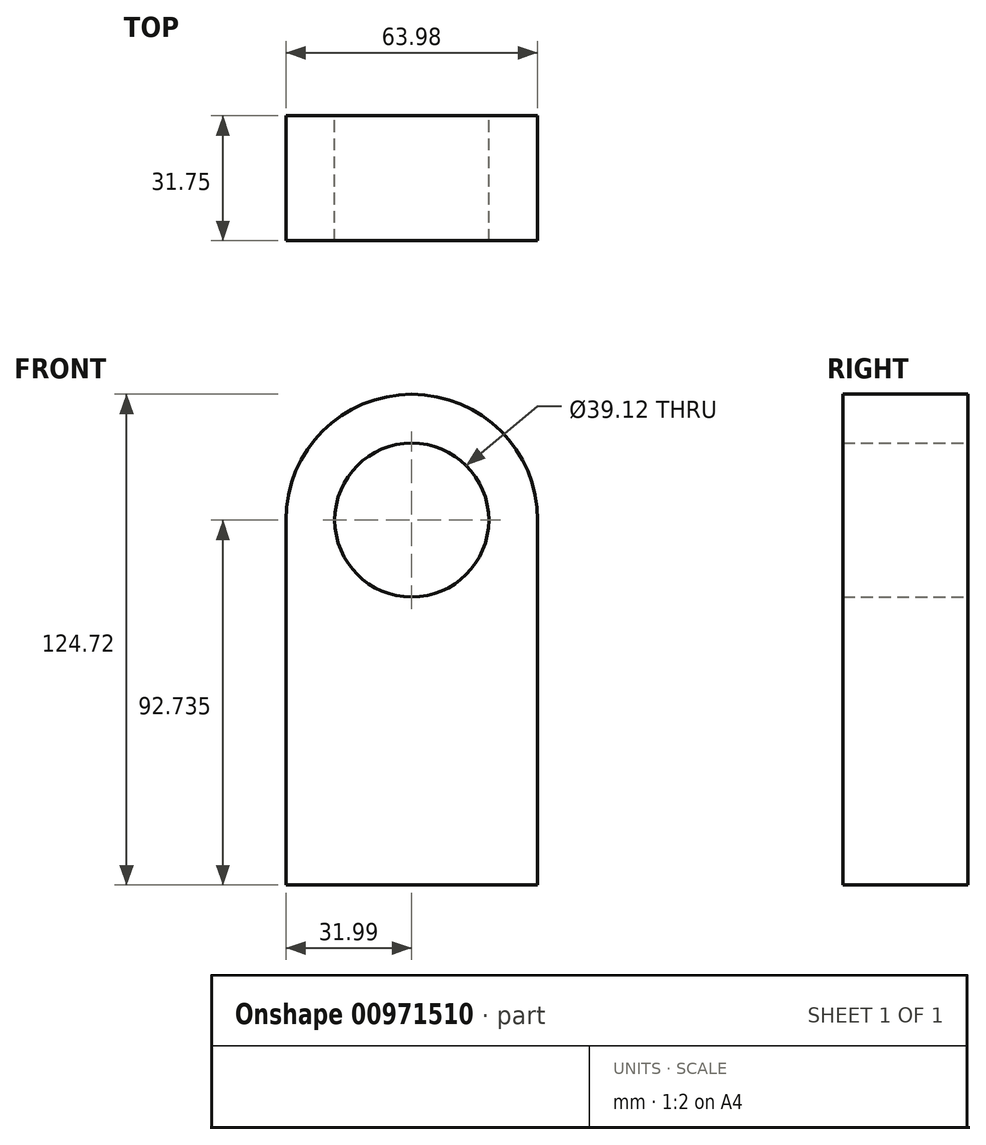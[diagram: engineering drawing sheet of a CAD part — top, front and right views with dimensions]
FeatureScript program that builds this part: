
annotation { "Feature Type Name" : "Feature", "Feature Type Description" : "" }
export const myFeature = defineFeature(function(context is Context, id is Id, definition is map)
    precondition{}
    {
        {
            var Q0;
            Q0=qCreatedBy(makeId("Front.planeOp"),FACE);
            var sketch = newSketch(context, id + "F0", { "sketchPlane" : qUnion([Q0])});
            skLineSegment(sketch, "E0.top", {"start": v(-31.99, -46.37) * mm, "end": v(31.99, -46.37) * mm});
            skLineSegment(sketch, "E0.left", {"start": v(-31.99, 46.37) * mm, "end": v(-31.99, -46.37) * mm});
            skLineSegment(sketch, "E0.right", {"start": v(31.99, 46.37) * mm, "end": v(31.99, -46.37) * mm});
            skPoint(sketch, "E0.middle", {"position": v(0, 0) * mm});
            skArc(sketch, "E1", {"start": v(31.99, 46.37) * mm, "mid": v(0, 78.35) * mm, "end": v(-31.99, 46.37) * mm});
            skCircle(sketch, "E2", {"center": v(0, 46.37) * mm, "radius": 19.56 * mm});
            skSolve(sketch);
        }
        {
            var Q0;
            Q0 = qSketchRegion(id + "F0", true);
            extrude(context, id + "F1", {"entities" : qUnion([Q0]), "depth" : 31.75 * mm, "offsetDistance" : 25.4 * mm});
        }
    });
